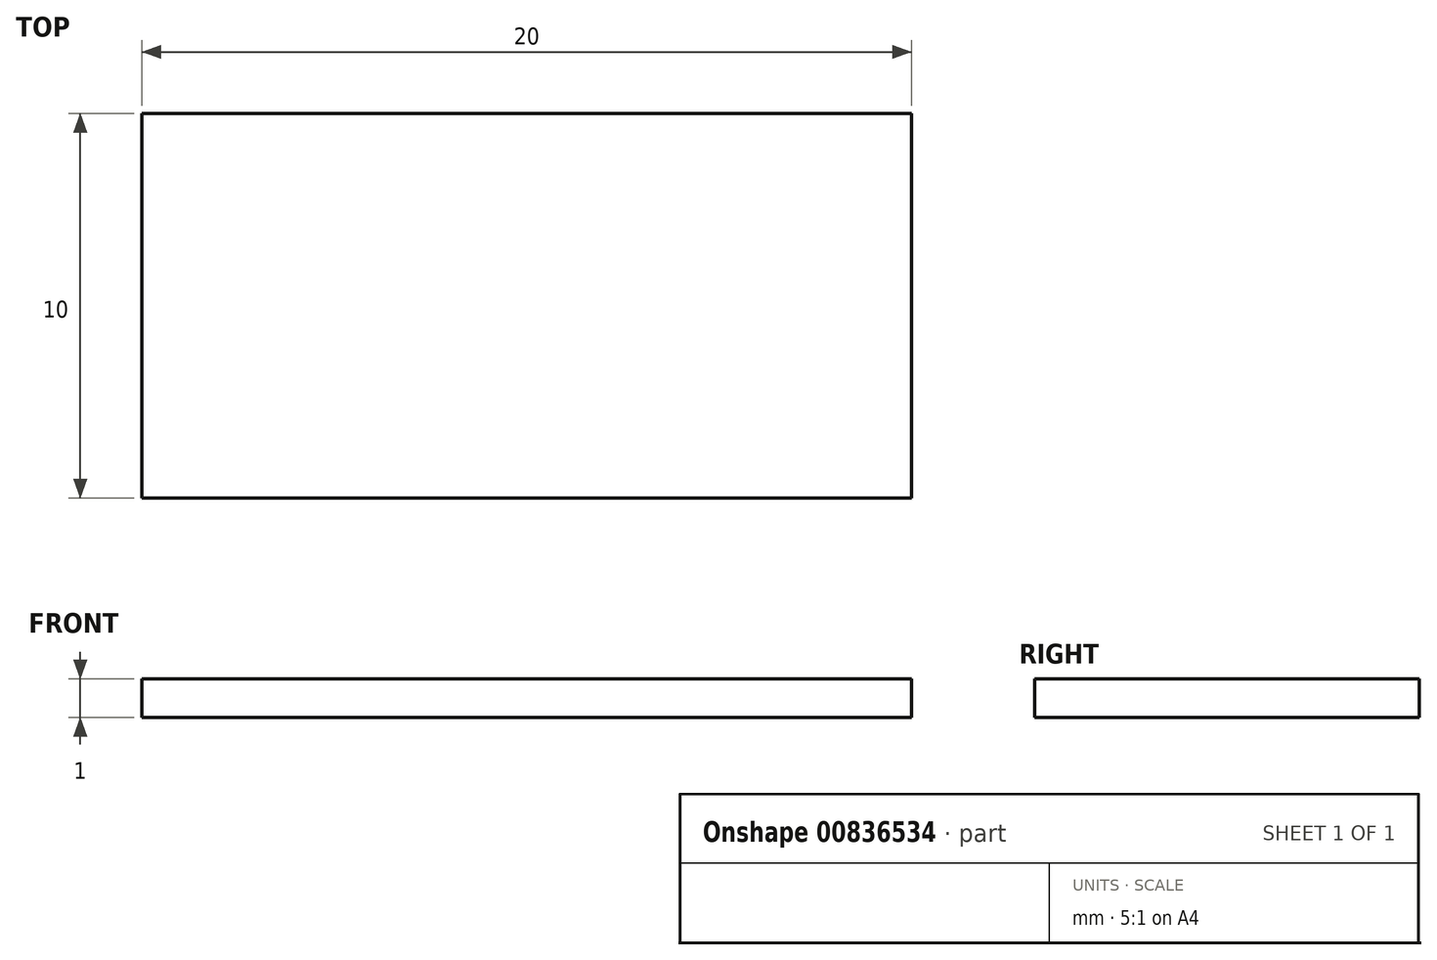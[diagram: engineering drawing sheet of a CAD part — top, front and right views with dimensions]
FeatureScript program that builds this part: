
annotation { "Feature Type Name" : "Feature", "Feature Type Description" : "" }
export const myFeature = defineFeature(function(context is Context, id is Id, definition is map)
    precondition{}
    {
        {
            var Q0;
            Q0=qCreatedBy(makeId("Top.planeOp"),FACE);
            var sketch = newSketch(context, id + "F0", { "sketchPlane" : qUnion([Q0])});
            skLineSegment(sketch, "E0.bottom", {"start": v(0, 0) * mm, "end": v(20, 0) * mm});
            skLineSegment(sketch, "E0.top", {"start": v(0, -10) * mm, "end": v(20, -10) * mm});
            skLineSegment(sketch, "E0.left", {"start": v(0, 0) * mm, "end": v(0, -10) * mm});
            skLineSegment(sketch, "E0.right", {"start": v(20, 0) * mm, "end": v(20, -10) * mm});
            skSolve(sketch);
        }
        {
            var Q0;
            Q0=makeQuery(id+"F0.imprint","IMPRINT",FACE,{"disambiguationData":[TD([[makeQuery(id+"F0.imprint","IMPRINT",EDGE,{"derivedFrom":sQuery(id+"F0.wireOp",EDGE,"E0.bottom")}),-1.0]])]});
            extrude(context, id + "F1", {"entities" : qUnion([Q0]), "depth" : 1 * mm, "offsetDistance" : 25 * mm});
        }
    });
